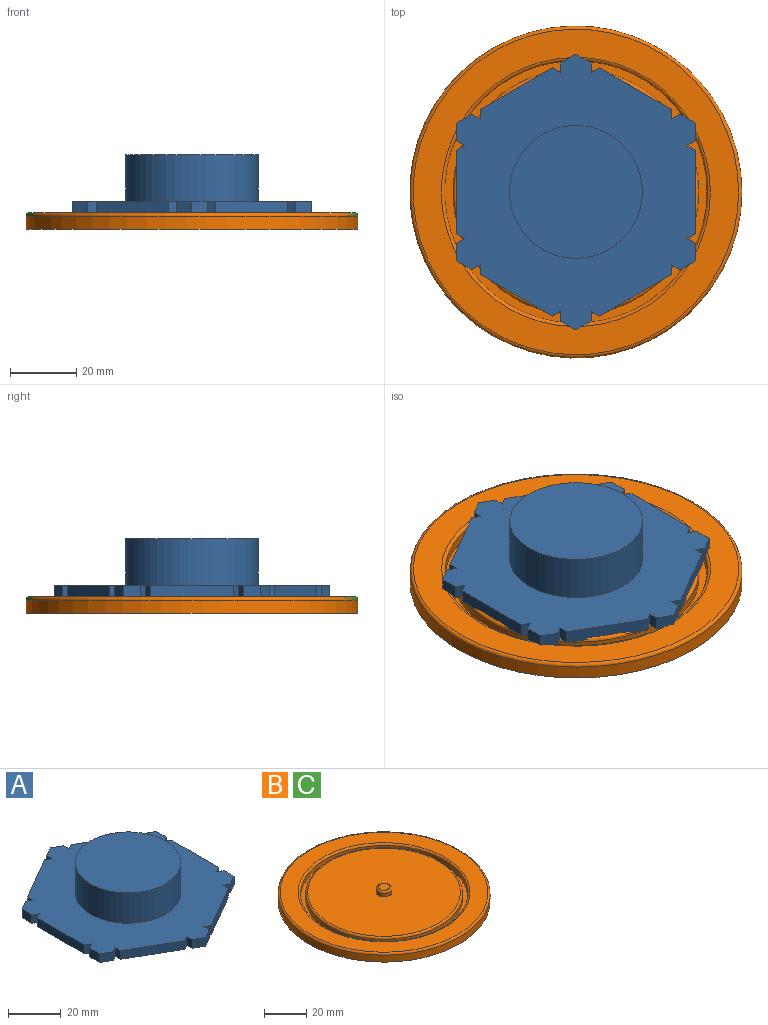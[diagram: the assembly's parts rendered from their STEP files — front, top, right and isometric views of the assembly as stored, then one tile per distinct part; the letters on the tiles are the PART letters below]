
ASSEMBLY  parts=3 mates=1
PART A: 48 faces, bbox 71.9x83x18 mm
  f0: plane 4x2.49mm, normal (0.5,0.87,0), area 11.5mm2, adj f1,f41,f42,f43
  f1: plane 4x2.49mm, normal (0.5,-0.87,0), area 11.5mm2, adj f0,f2,f42,f43
  f2: plane 25.12x4mm, normal (1,0,0), area 100.5mm2, adj f1,f3,f42,f43
  f3: plane 4x2.5mm, normal (0.5,0.87,0), area 11.5mm2, adj f2,f4,f42,f43
  f4: plane 4x2.5mm, normal (0.5,-0.87,0), area 11.5mm2, adj f3,f5,f42,f43
  f5: plane 5.31x4mm, normal (1,0,0), area 21.2mm2, adj f4,f6,f42,f43
  f6: plane 4.6x4mm, normal (0.5,0.87,0), area 21.3mm2, adj f5,f7,f42,f43
  f7: plane 4x2.49mm, normal (-0.5,0.87,0), area 11.5mm2, adj f6,f8,f42,f43
  f8: plane 4x2.87mm, normal (1,0,0), area 11.5mm2, adj f7,f9,f42,f43
  f9: plane 21.75x12.56mm, normal (0.5,0.87,0), area 100.5mm2, adj f8,f10,f42,f43
  f10: plane 4x2.5mm, normal (-0.5,0.87,0), area 11.5mm2, adj f9,f11,f42,f43
  f11: plane 4x2.89mm, normal (1,0,0), area 11.5mm2, adj f10,f12,f42,f43
  f12: plane 4.6x4mm, normal (0.5,0.87,0), area 21.2mm2, adj f11,f13,f42,f43
  f13: plane 4.6x4mm, normal (-0.5,0.87,0), area 21.3mm2, adj f12,f14,f42,f43
  f14: plane 4x2.87mm, normal (-1,0,0), area 11.5mm2, adj f13,f15,f42,f43
  f15: plane 4x2.49mm, normal (0.5,0.87,0), area 11.5mm2, adj f14,f16,f42,f43
  f16: plane 21.75x12.56mm, normal (-0.5,0.87,0), area 100.5mm2, adj f15,f17,f42,f43
  f17: plane 4x2.89mm, normal (-1,0,0), area 11.5mm2, adj f16,f18,f42,f43
  f18: plane 4x2.5mm, normal (0.5,0.87,0), area 11.5mm2, adj f17,f19,f42,f43
  f19: plane 4.6x4mm, normal (-0.5,0.87,0), area 21.2mm2, adj f18,f20,f42,f43
  f20: plane 5.31x4mm, normal (-1,0,0), area 21.3mm2, adj f19,f21,f42,f43
  f21: plane 4x2.49mm, normal (-0.5,-0.87,0), area 11.5mm2, adj f20,f22,f42,f43
  f22: plane 4x2.49mm, normal (-0.5,0.87,0), area 11.5mm2, adj f21,f23,f42,f43
  f23: plane 25.12x4mm, normal (-1,0,0), area 100.5mm2, adj f22,f24,f42,f43
  f24: plane 4x2.5mm, normal (-0.5,-0.87,0), area 11.5mm2, adj f23,f25,f42,f43
  f25: plane 4x2.5mm, normal (-0.5,0.87,0), area 11.5mm2, adj f24,f26,f42,f43
  f26: plane 5.31x4mm, normal (-1,0,0), area 21.2mm2, adj f25,f27,f42,f43
  f27: plane 4.6x4mm, normal (-0.5,-0.87,0), area 21.3mm2, adj f26,f28,f42,f43
  f28: plane 4x2.49mm, normal (0.5,-0.87,0), area 11.5mm2, adj f27,f29,f42,f43
  f29: plane 4x2.87mm, normal (-1,0,0), area 11.5mm2, adj f28,f30,f42,f43
  f30: plane 21.75x12.56mm, normal (-0.5,-0.87,0), area 100.5mm2, adj f29,f31,f42,f43
  f31: plane 4x2.5mm, normal (0.5,-0.87,0), area 11.5mm2, adj f30,f32,f42,f43
  f32: plane 4x2.89mm, normal (-1,0,0), area 11.5mm2, adj f31,f33,f42,f43
  f33: plane 4.6x4mm, normal (-0.5,-0.87,0), area 21.2mm2, adj f32,f34,f42,f43
  f34: plane 4.6x4mm, normal (0.5,-0.87,0), area 21.3mm2, adj f33,f35,f42,f43
  f35: plane 4x2.87mm, normal (1,0,0), area 11.5mm2, adj f34,f36,f42,f43
  f36: plane 4x2.49mm, normal (-0.5,-0.87,0), area 11.5mm2, adj f35,f37,f42,f43
  f37: plane 21.75x12.56mm, normal (0.5,-0.87,0), area 100.5mm2, adj f36,f38,f42,f43
  f38: plane 4x2.89mm, normal (1,0,0), area 11.5mm2, adj f37,f39,f42,f43
  f39: plane 4x2.5mm, normal (-0.5,-0.87,0), area 11.5mm2, adj f38,f40,f42,f43
  f40: plane 4.6x4mm, normal (0.5,-0.87,0), area 21.2mm2, adj f39,f41,f42,f43
  f41: plane 5.31x4mm, normal (1,0,0), area 21.3mm2, adj f0,f40,f42,f43
  f42: plane 83x71.88mm, normal (0,0,1), area 3174.8mm2, adj f0,f1,f2,f3,f4,f5,f6,f7
  f43: plane 83x71.88mm, normal (0,0,-1), area 4381.2mm2, adj f0,f1,f2,f3,f4,f5,f6,f7
  f44: cylinder r=20mm len=40mm, axis (0,0,-1), area 1759.3mm2, adj f42,f45
  f45: plane 40x40mm, normal (0,0,1), area 1256.6mm2, adj f44
  f46: cylinder r=4mm len=8mm, axis (0,0,-1), area 88mm2, adj f43,f47
  f47: plane 8x8mm, normal (0,0,-1), area 50.3mm2, adj f46
PART B: 13 faces, bbox 108.2x108.2x8 mm
  f0: plane 72x72mm, normal (0,0,1), area 4027.3mm2, adj f1,f11
  f1: cylinder r=3.75mm len=7.5mm, axis (0,0,-1), area 47.1mm2, adj f0,f3
  f2: plane 5.5x5.5mm, normal (0,0,1), area 23.8mm2, adj f3
  f3: torus R=2.75mm, axis (0,0,1), area 33.4mm2, adj f1,f2
  f4: cylinder r=37mm len=74mm, axis (0,0,1), area 581.2mm2, adj f6,f11
  f5: cylinder r=39.5mm len=79mm, axis (0,0,1), area 620.5mm2, adj f6,f12
  f6: plane 79x79mm, normal (0,0,1), area 600.8mm2, adj f4,f5
  f7: plane 100x100mm, normal (0,0,-1), area 7854mm2, adj f8
  f8: cylinder r=50mm len=100mm, axis (0,0,-1), area 1256.6mm2, adj f7,f9
  f9: torus R=49mm, axis (0,0,1), area 489.9mm2, adj f8,f10
  f10: plane 98x98mm, normal (0,0,1), area 2390mm2, adj f9,f12
  f11: torus R=36mm, axis (0,0,1), area 361.6mm2, adj f0,f4
  f12: torus R=40.5mm, axis (0,0,1), area 393.4mm2, adj f5,f10
PART C: same geometry as B
PLACE A t=(0,0,4.5)mm
PLACE B at identity
PLACE C at identity
MATE cylindrical A.f46 <-> C.f1  axis (0,0,-1) through (0,0,8)mm
